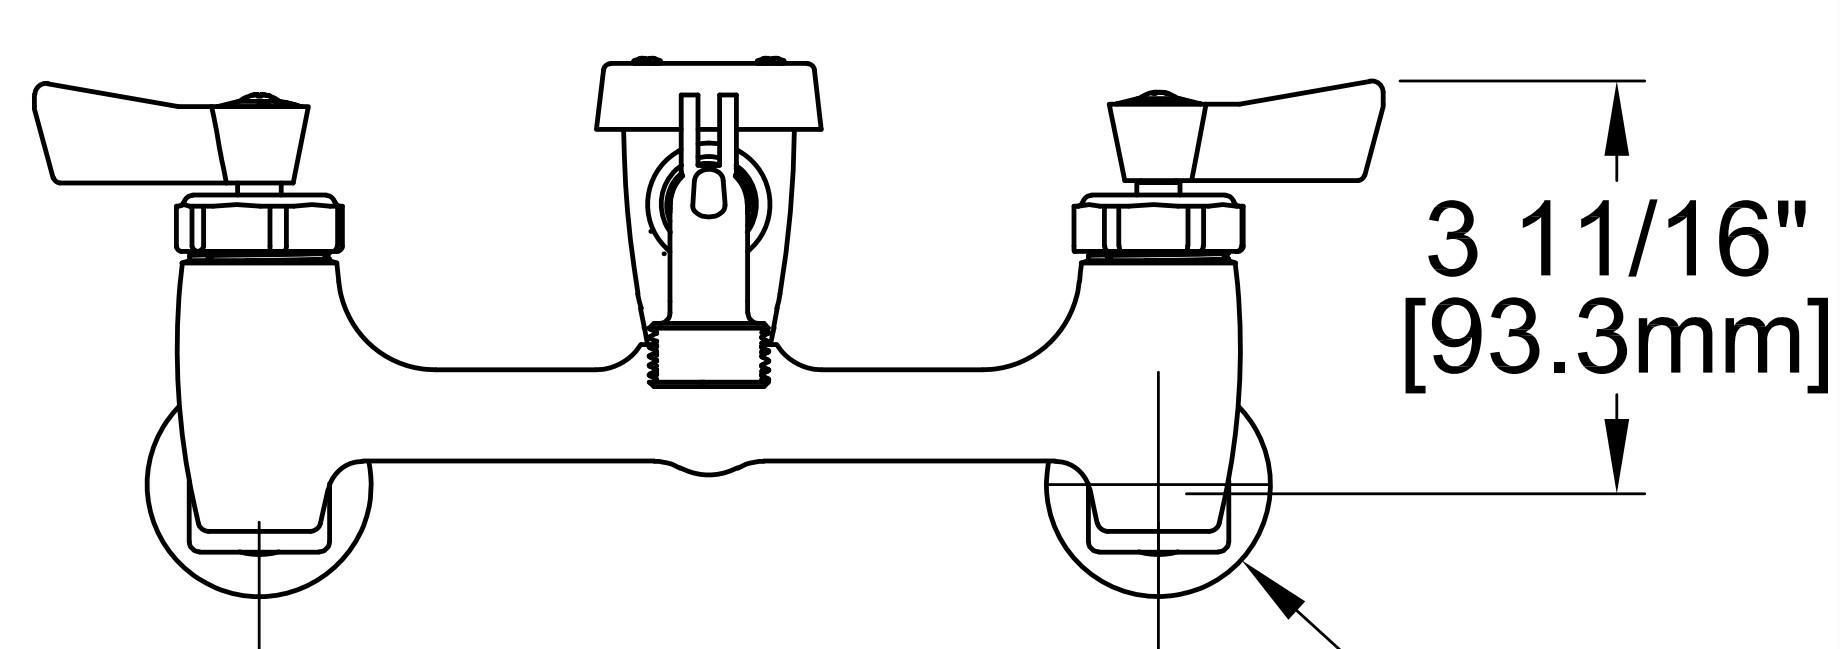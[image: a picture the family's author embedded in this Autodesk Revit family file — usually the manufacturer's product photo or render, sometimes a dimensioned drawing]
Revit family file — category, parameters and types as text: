
# Revit family: PRCB-SPA-SDDLL_34160
name_source: partatom
category: Plumbing Fixtures
units: mm (PartAtom-declared; Revit-internal decimal feet)

## family parameters
Always vertical = Yes
Cut with Voids When Loaded = No
OmniClass Number = 23.45.00.00
OmniClass Title = Sanitary, Laundry, and Cleaning Equipment
Part Type = Normal
Room Calculation Point = No
Round Connector Dimension = Use Diameter
Shared = No
Work Plane-Based = No

## types (1)
- PRCB-SPA-SDDLL_34160
    Cold Water Consumption = 0 GPM
    Cold Water Flow = 2 GPM
    Cold Water Maximum Pressure = 200.00 psi
    Cold Water Minimum Pressure = 80.00 psi
    Cold Water Size = 1/2"
    Cold Water Temperature Recommended = 40 °F
    Fixture Height = 4' - 0"
    Hot Water Consumption = 0 GPM
    Hot Water Flow = 2 GPM
    Hot Water Maximum Pressure = 200.00 psi
    Hot Water Minimum Pressure = 80.00 psi
    Hot Water Size = 1/2"
    Hot Water Temperature = 40 °F

## geometry (parser evidence)
native form markers: Sweep x66
no freeform markers — native parametric forms only
